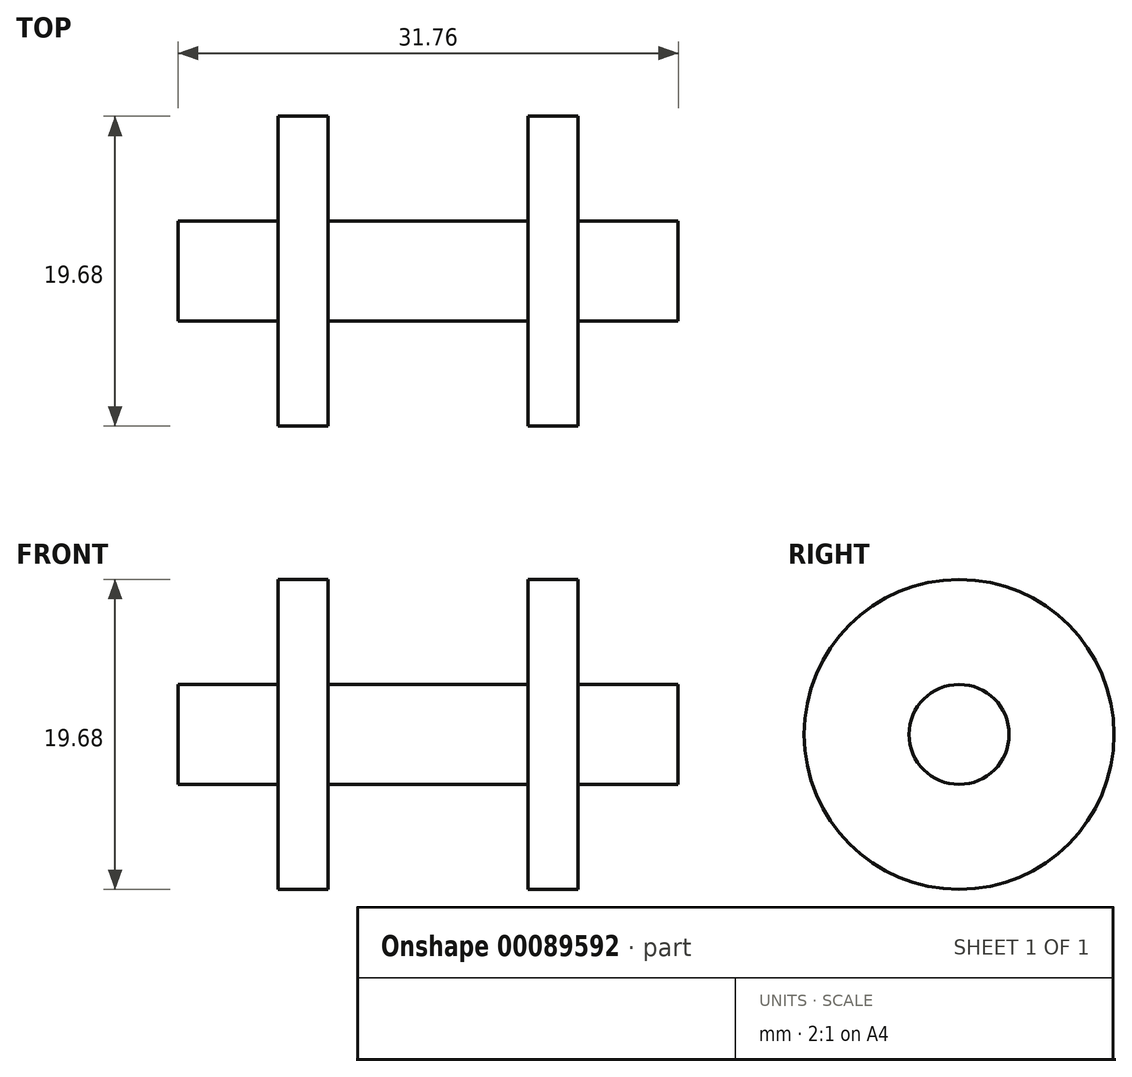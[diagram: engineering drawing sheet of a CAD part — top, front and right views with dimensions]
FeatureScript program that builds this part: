
annotation { "Feature Type Name" : "Feature", "Feature Type Description" : "" }
export const myFeature = defineFeature(function(context is Context, id is Id, definition is map)
    precondition{}
    {
        {
            var Q0;
            Q0=qCreatedBy(makeId("Top.planeOp"),FACE);
            var sketch = newSketch(context, id + "F0", { "sketchPlane" : qUnion([Q0])});
            skLineSegment(sketch, "E0", {"start": v(12.7, 0) * mm, "end": v(-12.7, 0) * mm});
            skLineSegment(sketch, "E1", {"start": v(-12.7, 0) * mm, "end": v(-12.7, 1.59) * mm});
            skLineSegment(sketch, "E2", {"start": v(-12.7, 1.59) * mm, "end": v(-9.53, 1.59) * mm});
            skLineSegment(sketch, "E3", {"start": v(-9.53, 1.59) * mm, "end": v(-9.53, 9.84) * mm});
            skLineSegment(sketch, "E4", {"start": v(-9.53, 9.84) * mm, "end": v(-6.35, 9.84) * mm});
            skLineSegment(sketch, "E5", {"start": v(-6.35, 9.84) * mm, "end": v(-6.35, 3.18) * mm});
            skLineSegment(sketch, "E6", {"start": v(-6.35, 3.17) * mm, "end": v(0, 3.18) * mm});
            skLineSegment(sketch, "E7.MirrorCS", {"start": v(6.35, 3.18) * mm, "end": v(0, 3.17) * mm});
            skLineSegment(sketch, "E8.MirrorCS", {"start": v(6.35, 9.84) * mm, "end": v(6.35, 3.18) * mm});
            skLineSegment(sketch, "E9.MirrorCS", {"start": v(9.53, 9.84) * mm, "end": v(6.35, 9.84) * mm});
            skLineSegment(sketch, "E10.MirrorCS", {"start": v(9.53, 1.59) * mm, "end": v(9.53, 9.84) * mm});
            skLineSegment(sketch, "E11.MirrorCS", {"start": v(12.7, 1.59) * mm, "end": v(9.53, 1.59) * mm});
            skLineSegment(sketch, "E12.MirrorCS", {"start": v(12.7, 0) * mm, "end": v(12.7, 1.59) * mm});
            skPoint(sketch, "E13", {"position": v(0, 0) * mm});
            skLineSegment(sketch, "E14", {"start": v(-9.53, 1.59) * mm, "end": v(9.53, 1.59) * mm, "construction": true});
            skPoint(sketch, "E15", {"position": v(0, 1.59) * mm});
            skSolve(sketch);
        }
        {
            var Q0;
            Q0=qCreatedBy(makeId("Right.planeOp"),FACE);
            var sketch = newSketch(context, id + "F1", { "sketchPlane" : qUnion([Q0])});
            skCircle(sketch, "E16", {"center": v(0, 0) * mm, "radius": 3.18 * mm});
            skSolve(sketch);
        }
        {
            var Q0;
            Q0=qSketchRegion(id+"F1",true);
            extrude(context, id + "F2", {"entities" : qUnion([Q0]), "endBound" : BoundingType.SYMMETRIC, "depth" : 31.75 * mm});
        }
        {
            var Q0;
            Q0=makeQuery(id+"F0.imprint","IMPRINT",FACE,{"disambiguationData":[TD([[makeQuery(id+"F0.imprint","IMPRINT",EDGE,{"derivedFrom":sQuery(id+"F0.wireOp",EDGE,"E0")}),-1.0]])]});
            var Q1;
            Q1=makeQuery(id+"F2.opExtrude","SWEPT_FACE",FACE,{"disambiguationData":[OSD([sQuery(id+"F1.wireOp",EDGE,"E16")])]});
            revolve(context, id + "F3", {"operationType" : NewBodyOperationType.ADD, "entities" : qUnion([Q0]), "axis" : qUnion([Q1]), "revolveType" : RevolveType.FULL});
        }
    });
